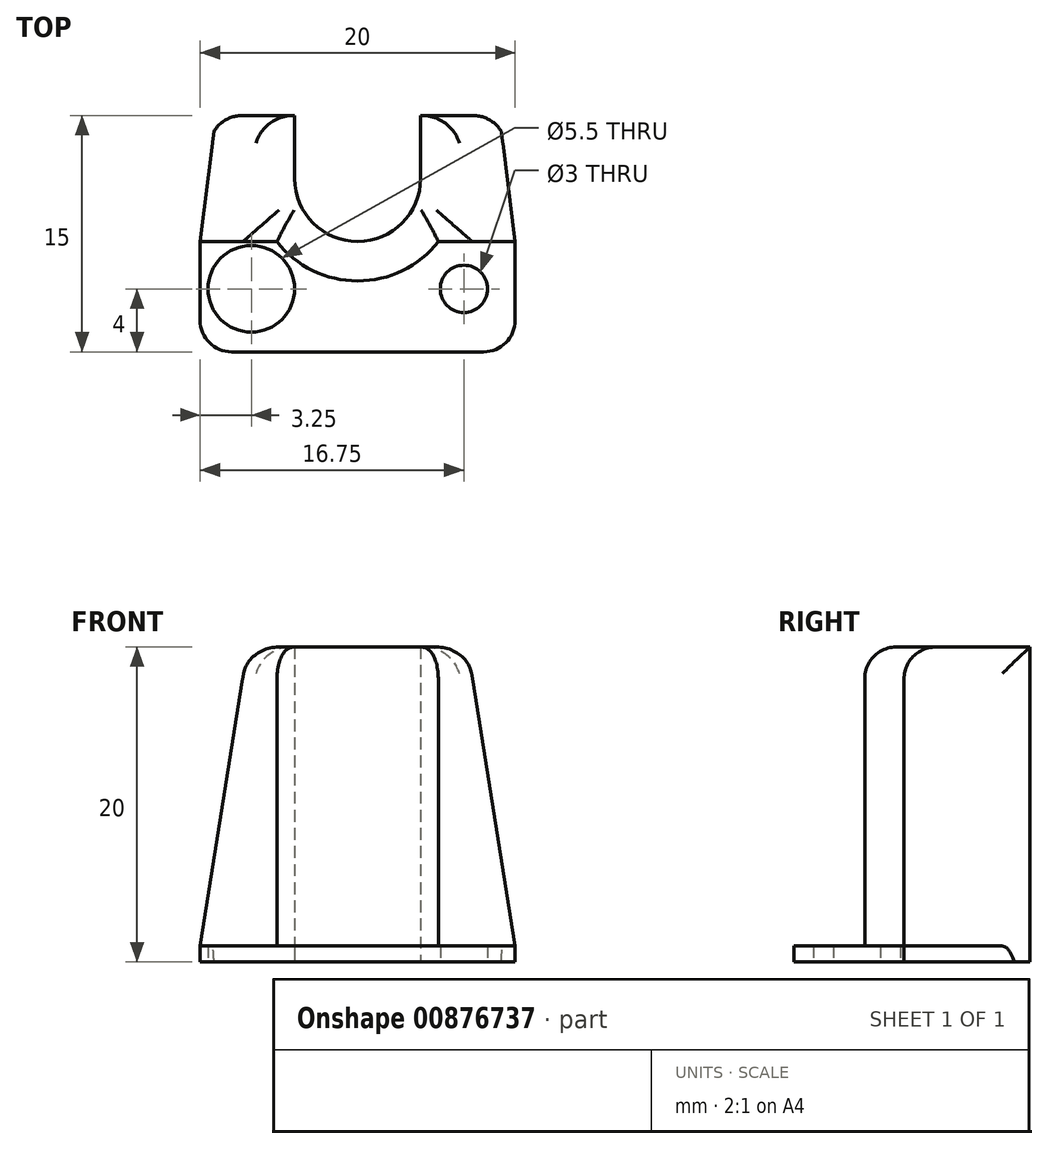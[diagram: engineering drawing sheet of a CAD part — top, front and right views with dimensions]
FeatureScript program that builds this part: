
annotation { "Feature Type Name" : "Feature", "Feature Type Description" : "" }
export const myFeature = defineFeature(function(context is Context, id is Id, definition is map)
    precondition{}
    {
        {
            var Q0;
            Q0=qCreatedBy(makeId("Top.planeOp"),FACE);
            var sketch = newSketch(context, id + "F0", { "sketchPlane" : qUnion([Q0])});
            skArc(sketch, "E0", {"start": v(-4, 0) * mm, "mid": v(0, -4) * mm, "end": v(4, 0) * mm});
            skCircle(sketch, "E1", {"center": v(6.75, -7) * mm, "radius": 2.75 * mm});
            skLineSegment(sketch, "E2", {"start": v(0, 0) * mm, "end": v(0, -16.54) * mm, "construction": true});
            skLineSegment(sketch, "E3", {"start": v(9.5, -5.45) * mm, "end": v(9.5, -18.9) * mm, "construction": true});
            skLineSegment(sketch, "E4", {"start": v(-11.5, 4) * mm, "end": v(16.34, 4) * mm, "construction": true});
            skLineSegment(sketch, "E5", {"start": v(-4.1, -9.75) * mm, "end": v(25.8, -9.75) * mm, "construction": true});
            skCircle(sketch, "E6.MirrorC", {"center": v(-6.75, -7) * mm, "radius": 2.75 * mm});
            skCircle(sketch, "E7", {"center": v(6.75, -7) * mm, "radius": 1.5 * mm});
            skCircle(sketch, "E8.MirrorC", {"center": v(-6.75, -7) * mm, "radius": 1.5 * mm});
            skLineSegment(sketch, "E9", {"start": v(4, 0) * mm, "end": v(4, 4) * mm});
            skLineSegment(sketch, "E10", {"start": v(4, 4) * mm, "end": v(9, 4) * mm});
            skLineSegment(sketch, "E11", {"start": v(9, 4) * mm, "end": v(10, -4) * mm});
            skLineSegment(sketch, "E12", {"start": v(10, -4) * mm, "end": v(10, -11) * mm});
            skLineSegment(sketch, "E13", {"start": v(10, -11) * mm, "end": v(0, -11) * mm});
            skLineSegment(sketch, "E14.MirrorCS", {"start": v(-4, 0) * mm, "end": v(-4, 4) * mm});
            skLineSegment(sketch, "E15.MirrorCS", {"start": v(-9, 4) * mm, "end": v(-10, -4) * mm});
            skLineSegment(sketch, "E16.MirrorCS", {"start": v(-10, -4) * mm, "end": v(-10, -11) * mm});
            skLineSegment(sketch, "E17.MirrorCS", {"start": v(-10, -11) * mm, "end": v(0, -11) * mm});
            skLineSegment(sketch, "E18", {"start": v(-9, 4) * mm, "end": v(-4, 4) * mm});
            skArc(sketch, "E19", {"start": v(-6.5, 0) * mm, "mid": v(0, -6.5) * mm, "end": v(6.5, 0) * mm});
            skLineSegment(sketch, "E20", {"start": v(-6.5, 0) * mm, "end": v(-6.5, 4) * mm});
            skLineSegment(sketch, "E21", {"start": v(6.5, 0) * mm, "end": v(6.5, 4) * mm});
            skLineSegment(sketch, "E22", {"start": v(10, -4) * mm, "end": v(5.12, -4) * mm});
            skLineSegment(sketch, "E23.MirrorCS", {"start": v(-10, -4) * mm, "end": v(-5.12, -4) * mm});
            skSolve(sketch);
        }
        {
            var Q0;
            Q0=makeQuery(id+"F0.imprint","IMPRINT",FACE,{"disambiguationData":[TD([[makeQuery(id+"F0.imprint","IMPRINT",EDGE,{"derivedFrom":sQuery(id+"F0.wireOp",EDGE,"E1")}),-1.0]])]});
            var Q1;
            Q1=makeQuery(id+"F0.imprint","IMPRINT",FACE,{"disambiguationData":[TD([[makeQuery(id+"F0.imprint","IMPRINT",EDGE,{"derivedFrom":sQuery(id+"F0.wireOp",EDGE,"E6.MirrorC")}),-1.0]])]});
            var Q2;
            Q2=makeQuery(id+"F0.imprint","IMPRINT",FACE,{"disambiguationData":[TD([[makeQuery(id+"F0.imprint","IMPRINT",EDGE,{"derivedFrom":sQuery(id+"F0.wireOp",EDGE,"E1")}),1.0]])]});
            extrude(context, id + "F1", {"entities" : qUnion([Q0, Q1, Q2]), "depth" : 1 * mm, "offsetDistance" : 25 * mm});
        }
        {
            var Q0;
            Q0=makeQuery(id+"F0.imprint","IMPRINT",FACE,{"disambiguationData":[TD([[makeQuery(id+"F0.imprint","IMPRINT",EDGE,{"derivedFrom":sQuery(id+"F0.wireOp",EDGE,"E0")}),-1.0]])]});
            var Q1;
            {var subQ2=sQuery(id+"F0.wireOp",EDGE,"E15.MirrorCS");Q1=makeQuery(id+"F0.imprint","IMPRINT",FACE,{"disambiguationData":[TD([[makeQuery(id+"F0.imprint","IMPRINT",EDGE,{"derivedFrom":subQ2}),1.0]])]});}
            var Q2;
            {var subQ3=sQuery(id+"F0.wireOp",EDGE,"E11");Q2=makeQuery(id+"F0.imprint","IMPRINT",FACE,{"disambiguationData":[TD([[makeQuery(id+"F0.imprint","IMPRINT",EDGE,{"derivedFrom":subQ3}),-1.0]])]});}
            extrude(context, id + "F2", {"entities" : qUnion([Q0, Q1, Q2]), "operationType" : NewBodyOperationType.ADD, "depth" : 20 * mm, "offsetDistance" : 25 * mm});
        }
        {
            var Q0;
            Q0=makeQuery(id+"F2.opExtrude","CAP_EDGE",EDGE,{"disambiguationData":[OSD([sQuery(id+"F0.wireOp",EDGE,"E15.MirrorCS")])],"isStart":false});
            var Q1;
            Q1=makeQuery(id+"F2.opExtrude","CAP_EDGE",EDGE,{"disambiguationData":[OSD([sQuery(id+"F0.wireOp",EDGE,"E11")])],"isStart":false});
            chamfer(context, id + "F3", {"entities" : qUnion([Q0, Q1]), "chamferType" : ChamferType.TWO_OFFSETS, "width1" : 3 * mm, "oppositeDirection" : false, "width2" : 19 * mm, "tangentPropagation" : true});
        }
        {
            var Q0;
            Q0=makeQuery(id+"F2.opExtrude","CAP_EDGE",EDGE,{"disambiguationData":[OSD([sQuery(id+"F0.wireOp",EDGE,"E19")])],"isStart":false});
            var Q1;
            Q1=makeQuery(id+"F2.opExtrude","CAP_EDGE",EDGE,{"disambiguationData":[OSD([sQuery(id+"F0.wireOp",EDGE,"E23.MirrorCS")])],"isStart":false});
            var Q2;
            Q2=makeQuery(id+"F2.opExtrude","CAP_EDGE",EDGE,{"disambiguationData":[OSD([sQuery(id+"F0.wireOp",EDGE,"E22")])],"isStart":false});
            var Q3;
            {var subQ0=sQuery(id+"F0.wireOp",EDGE,"E15.MirrorCS");Q3=makeQuery(id+"F3.opChamfer","BLEND_EDGE",EDGE,{"blendedFrom":[makeQuery(id+"F2.opExtrude","CAP_EDGE",EDGE,{"disambiguationData":[OSD([subQ0])],"isStart":false}),makeQuery(id+"F2.opExtrude","CAP_FACE",FACE,{"disambiguationData":[OSD([sQuery(id+"F0.wireOp",EDGE,"E0"),sQuery(id+"F0.wireOp",EDGE,"E9"),sQuery(id+"F0.wireOp",EDGE,"E10"),sQuery(id+"F0.wireOp",EDGE,"E11"),sQuery(id+"F0.wireOp",EDGE,"E14.MirrorCS"),subQ0,sQuery(id+"F0.wireOp",EDGE,"E18"),sQuery(id+"F0.wireOp",EDGE,"E19"),sQuery(id+"F0.wireOp",EDGE,"E22"),sQuery(id+"F0.wireOp",EDGE,"E23.MirrorCS")])],"isStart":false})],"blendedInto":[makeQuery(id+"F2.opExtrude","CAP_FACE",FACE,{"disambiguationData":[OSD([sQuery(id+"F0.wireOp",EDGE,"E0"),sQuery(id+"F0.wireOp",EDGE,"E9"),sQuery(id+"F0.wireOp",EDGE,"E10"),sQuery(id+"F0.wireOp",EDGE,"E11"),sQuery(id+"F0.wireOp",EDGE,"E14.MirrorCS"),subQ0,sQuery(id+"F0.wireOp",EDGE,"E18"),sQuery(id+"F0.wireOp",EDGE,"E19"),sQuery(id+"F0.wireOp",EDGE,"E22"),sQuery(id+"F0.wireOp",EDGE,"E23.MirrorCS")])],"isStart":false})]});}
            var Q4;
            {var subQ0=sQuery(id+"F0.wireOp",EDGE,"E11");Q4=makeQuery(id+"F3.opChamfer","BLEND_EDGE",EDGE,{"blendedFrom":[makeQuery(id+"F2.opExtrude","CAP_EDGE",EDGE,{"disambiguationData":[OSD([subQ0])],"isStart":false}),makeQuery(id+"F2.opExtrude","CAP_FACE",FACE,{"disambiguationData":[OSD([sQuery(id+"F0.wireOp",EDGE,"E0"),sQuery(id+"F0.wireOp",EDGE,"E9"),sQuery(id+"F0.wireOp",EDGE,"E10"),subQ0,sQuery(id+"F0.wireOp",EDGE,"E14.MirrorCS"),sQuery(id+"F0.wireOp",EDGE,"E15.MirrorCS"),sQuery(id+"F0.wireOp",EDGE,"E18"),sQuery(id+"F0.wireOp",EDGE,"E19"),sQuery(id+"F0.wireOp",EDGE,"E22"),sQuery(id+"F0.wireOp",EDGE,"E23.MirrorCS")])],"isStart":false})],"blendedInto":[makeQuery(id+"F2.opExtrude","CAP_FACE",FACE,{"disambiguationData":[OSD([sQuery(id+"F0.wireOp",EDGE,"E0"),sQuery(id+"F0.wireOp",EDGE,"E9"),sQuery(id+"F0.wireOp",EDGE,"E10"),subQ0,sQuery(id+"F0.wireOp",EDGE,"E14.MirrorCS"),sQuery(id+"F0.wireOp",EDGE,"E15.MirrorCS"),sQuery(id+"F0.wireOp",EDGE,"E18"),sQuery(id+"F0.wireOp",EDGE,"E19"),sQuery(id+"F0.wireOp",EDGE,"E22"),sQuery(id+"F0.wireOp",EDGE,"E23.MirrorCS")])],"isStart":false})]});}
            var Q5;
            Q5=makeQuery(id+"F1.opExtrude","CAP_EDGE",EDGE,{"disambiguationData":[OSD([sQuery(id+"F0.wireOp",EDGE,"E23.MirrorCS")])],"isStart":false});
            var Q6;
            Q6=makeQuery(id+"F1.opExtrude","CAP_EDGE",EDGE,{"disambiguationData":[OSD([sQuery(id+"F0.wireOp",EDGE,"E19")])],"isStart":false});
            var Q7;
            Q7=makeQuery(id+"F1.opExtrude","CAP_EDGE",EDGE,{"disambiguationData":[OSD([sQuery(id+"F0.wireOp",EDGE,"E22")])],"isStart":false});
            var Q8;
            Q8=makeQuery(id+"F1.opExtrude","SWEPT_EDGE",EDGE,{"disambiguationData":[OSD([sQuery(id+"F0.wireOp",EDGE,"E12"),sQuery(id+"F0.wireOp",EDGE,"E13")])]});
            var Q9;
            Q9=makeQuery(id+"F1.opExtrude","SWEPT_EDGE",EDGE,{"disambiguationData":[OSD([sQuery(id+"F0.wireOp",EDGE,"E16.MirrorCS"),sQuery(id+"F0.wireOp",EDGE,"E17.MirrorCS")])]});
            var Q10;
            Q10=makeQuery(id+"F3.opChamfer","BLEND_EDGE",EDGE,{"blendedFrom":[makeQuery(id+"F2.opExtrude","CAP_EDGE",EDGE,{"disambiguationData":[OSD([sQuery(id+"F0.wireOp",EDGE,"E15.MirrorCS")])],"isStart":false}),makeQuery(id+"F2.opExtrude","SWEPT_FACE",FACE,{"disambiguationData":[OSD([sQuery(id+"F0.wireOp",EDGE,"E18")])]})],"blendedInto":[makeQuery(id+"F2.opExtrude","SWEPT_FACE",FACE,{"disambiguationData":[OSD([sQuery(id+"F0.wireOp",EDGE,"E18")])]})]});
            var Q11;
            Q11=makeQuery(id+"F3.opChamfer","BLEND_EDGE",EDGE,{"blendedFrom":[makeQuery(id+"F2.opExtrude","CAP_EDGE",EDGE,{"disambiguationData":[OSD([sQuery(id+"F0.wireOp",EDGE,"E11")])],"isStart":false}),makeQuery(id+"F2.opExtrude","SWEPT_FACE",FACE,{"disambiguationData":[OSD([sQuery(id+"F0.wireOp",EDGE,"E10")])]})],"blendedInto":[makeQuery(id+"F2.opExtrude","SWEPT_FACE",FACE,{"disambiguationData":[OSD([sQuery(id+"F0.wireOp",EDGE,"E10")])]})]});
            fillet(context, id + "F4", {"entities" : qUnion([Q0, Q1, Q2, Q3, Q4, Q5, Q6, Q7, Q8, Q9, Q10, Q11]), "radius" : 2 * mm, "tangentPropagation" : true, "allowEdgeOverflow" : false});
        }
    });
